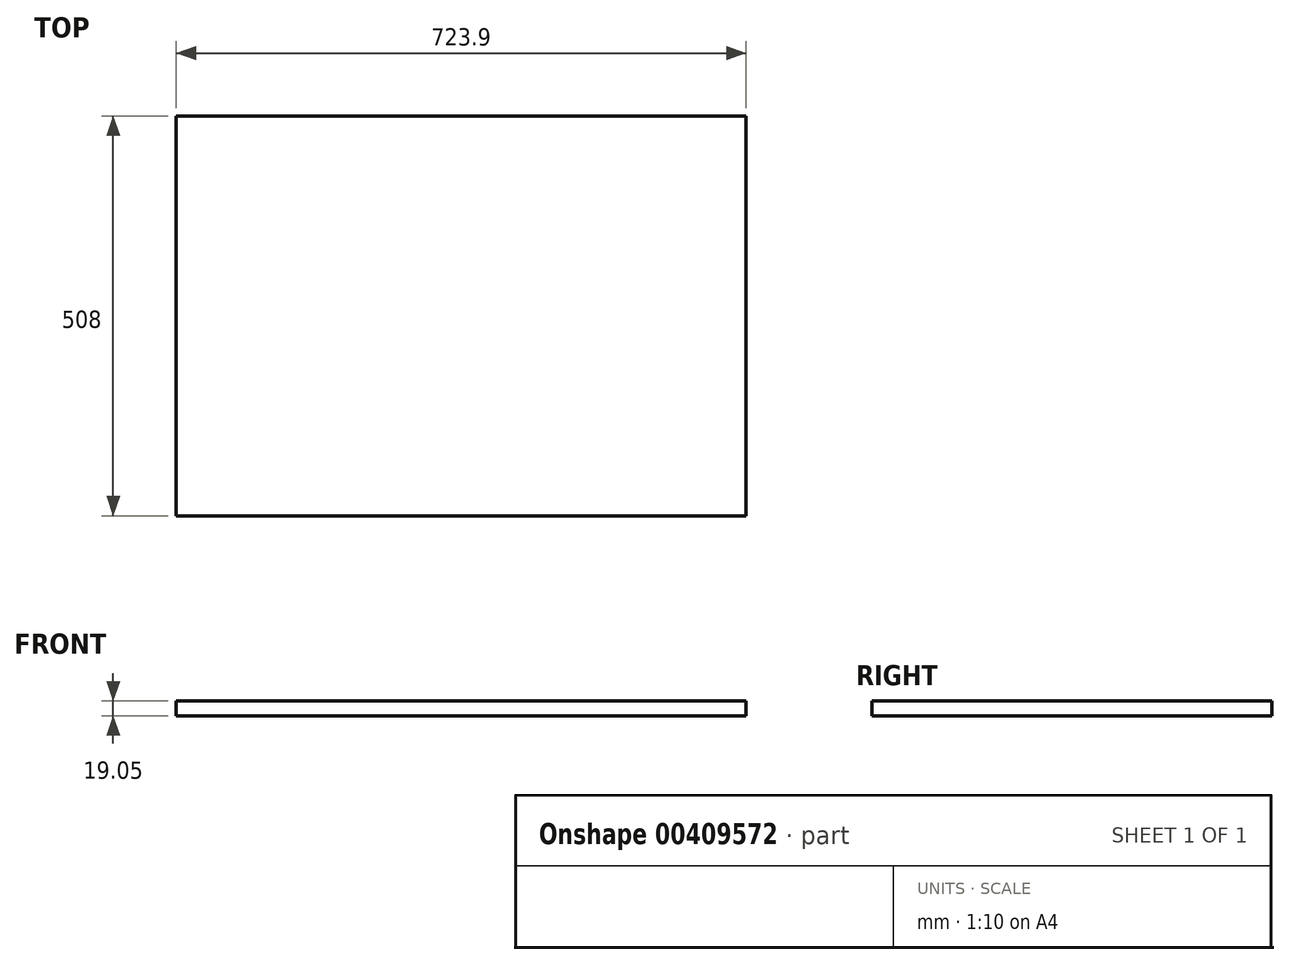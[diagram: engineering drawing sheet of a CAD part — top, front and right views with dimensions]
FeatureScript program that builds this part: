
annotation { "Feature Type Name" : "Feature", "Feature Type Description" : "" }
export const myFeature = defineFeature(function(context is Context, id is Id, definition is map)
    precondition{}
    {
        {
            var Q0;
            Q0=qCreatedBy(makeId("Top.planeOp"),FACE);
            var sketch = newSketch(context, id + "F0", { "sketchPlane" : qUnion([Q0])});
            skLineSegment(sketch, "E0.bottom", {"start": v(-454.84, 331.05) * mm, "end": v(269.06, 331.05) * mm});
            skLineSegment(sketch, "E0.top", {"start": v(-454.84, -176.95) * mm, "end": v(269.06, -176.95) * mm});
            skLineSegment(sketch, "E0.left", {"start": v(-454.84, 331.05) * mm, "end": v(-454.84, -176.95) * mm});
            skLineSegment(sketch, "E0.right", {"start": v(269.06, 331.05) * mm, "end": v(269.06, -176.95) * mm});
            skSolve(sketch);
        }
        {
            var Q0;
            Q0=makeQuery(id+"F0.imprint","IMPRINT",FACE,{"disambiguationData":[TD([[makeQuery(id+"F0.imprint","IMPRINT",EDGE,{"derivedFrom":sQuery(id+"F0.wireOp",EDGE,"E0.bottom")}),-1.0]])]});
            extrude(context, id + "F1", {"entities" : qUnion([Q0]), "depth" : 19.05 * mm});
        }
    });
